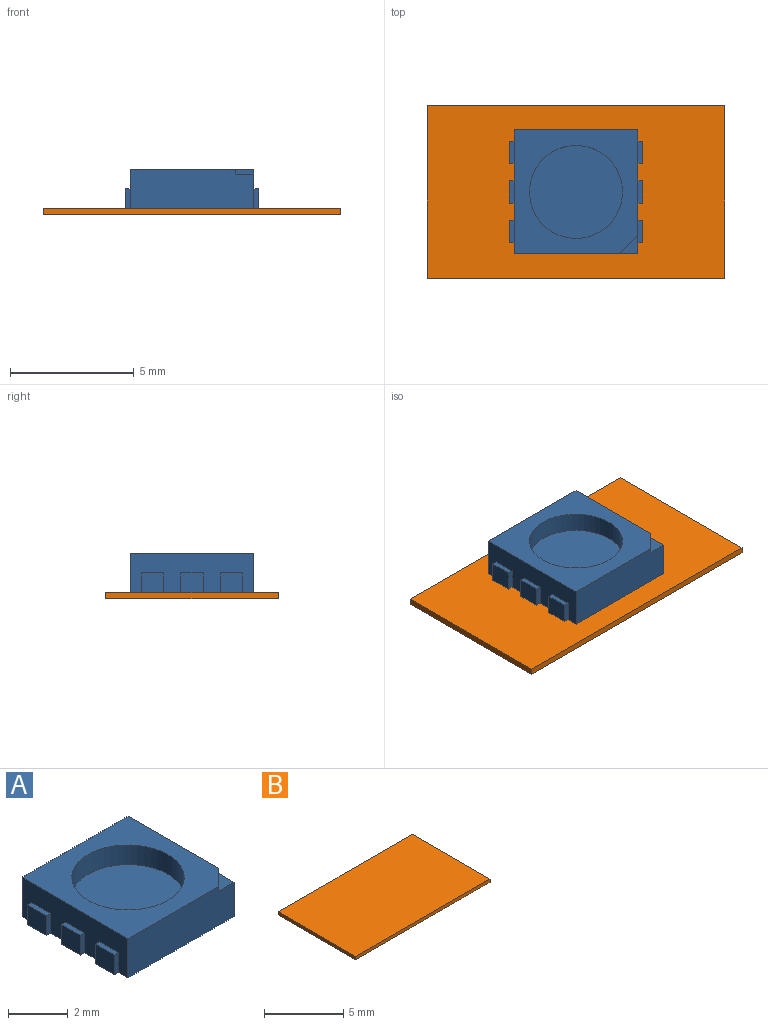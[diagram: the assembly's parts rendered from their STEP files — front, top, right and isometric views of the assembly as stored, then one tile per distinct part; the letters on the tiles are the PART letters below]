
ASSEMBLY  parts=2 mates=1
PART A: 34 faces, bbox 5.4x5x1.6 mm
  f0: plane 5x1.6mm, normal (1,0,0), area 5.7mm2, adj f1,f2,f4,f5,f18,f19,f21,f22
  f1: plane 5x1.6mm, normal (0,-1,0), area 7.9mm2, adj f0,f2,f3,f5,f30,f31
  f2: plane 5x5mm, normal (0,0,1), area 13.7mm2, adj f0,f1,f3,f4,f30,f32
  f3: plane 5x1.6mm, normal (-1,0,0), area 5.8mm2, adj f1,f2,f4,f5,f6,f7,f8,f10
  f4: plane 5x1.6mm, normal (0,1,0), area 8mm2, adj f0,f2,f3,f5
  f5: plane 5.4x5mm, normal (0,0,-1), area 26.1mm2, adj f0,f1,f3,f4,f6,f7,f9,f11
  f6: plane 0.8x0.2mm, normal (0,-1,0), area 0.2mm2, adj f3,f5,f8,f9
  f7: plane 0.8x0.2mm, normal (0,1,0), area 0.2mm2, adj f3,f5,f8,f9
  f8: plane 0.9x0.2mm, normal (0,0,1), area 0.2mm2, adj f3,f6,f7,f9
  f9: plane 0.9x0.8mm, normal (-1,0,0), area 0.7mm2, adj f5,f6,f7,f8
  f10: plane 0.9x0.2mm, normal (0,0,1), area 0.2mm2, adj f3,f11,f12,f13
  f11: plane 0.8x0.2mm, normal (0,1,0), area 0.2mm2, adj f3,f5,f10,f13
  f12: plane 0.8x0.2mm, normal (0,-1,0), area 0.2mm2, adj f3,f5,f10,f13
  f13: plane 0.9x0.8mm, normal (-1,0,0), area 0.7mm2, adj f5,f10,f11,f12
  f14: plane 0.9x0.2mm, normal (0,0,1), area 0.2mm2, adj f3,f15,f16,f17
  f15: plane 0.8x0.2mm, normal (0,1,0), area 0.2mm2, adj f3,f5,f14,f17
  f16: plane 0.8x0.2mm, normal (0,-1,0), area 0.2mm2, adj f3,f5,f14,f17
  f17: plane 0.9x0.8mm, normal (-1,0,0), area 0.7mm2, adj f5,f14,f15,f16
  f18: plane 0.8x0.2mm, normal (0,-1,0), area 0.2mm2, adj f0,f5,f20,f21
  f19: plane 0.8x0.2mm, normal (0,1,0), area 0.2mm2, adj f0,f5,f20,f21
  f20: plane 0.9x0.8mm, normal (1,0,0), area 0.7mm2, adj f5,f18,f19,f21
  f21: plane 0.9x0.2mm, normal (0,0,1), area 0.2mm2, adj f0,f18,f19,f20
  f22: plane 0.8x0.2mm, normal (0,-1,0), area 0.2mm2, adj f0,f5,f24,f25
  f23: plane 0.8x0.2mm, normal (0,1,0), area 0.2mm2, adj f0,f5,f24,f25
  f24: plane 0.9x0.8mm, normal (1,0,0), area 0.7mm2, adj f5,f22,f23,f25
  f25: plane 0.9x0.2mm, normal (0,0,1), area 0.2mm2, adj f0,f22,f23,f24
  f26: plane 0.8x0.2mm, normal (0,-1,0), area 0.2mm2, adj f0,f5,f28,f29
  f27: plane 0.8x0.2mm, normal (0,1,0), area 0.2mm2, adj f0,f5,f28,f29
  f28: plane 0.9x0.8mm, normal (1,0,0), area 0.7mm2, adj f5,f26,f27,f29
  f29: plane 0.9x0.2mm, normal (0,0,1), area 0.2mm2, adj f0,f26,f27,f28
  f30: plane 0.75x0.75mm, normal (0.71,-0.71,0), area 0.2mm2, adj f0,f1,f2,f31
  f31: plane 0.75x0.75mm, normal (0,0,1), area 0.3mm2, adj f0,f1,f30
  f32: cylinder r=1.88mm len=3.75mm, axis (0,0,1), area 9.4mm2, adj f2,f33
  f33: plane 3.75x3.75mm, normal (0,0,1), area 11mm2, adj f32
PART B: 6 faces, bbox 12x6.9x0.3 mm
  f0: plane 6.94x0.25mm, normal (1,0,0), area 1.7mm2, adj f1,f3,f4,f5
  f1: plane 12x0.25mm, normal (0,1,0), area 3mm2, adj f0,f2,f4,f5
  f2: plane 6.94x0.25mm, normal (-1,0,0), area 1.7mm2, adj f1,f3,f4,f5
  f3: plane 12x0.25mm, normal (0,-1,0), area 3mm2, adj f0,f2,f4,f5
  f4: plane 12x6.94mm, normal (0,0,1), area 83.3mm2, adj f0,f1,f2,f3
  f5: plane 12x6.94mm, normal (0,0,-1), area 83.3mm2, adj f0,f1,f2,f3
PLACE A t=(4.9,5.07,2.56)mm
PLACE B t=(4.9,5.07,2.31)mm
MATE planar B.f4 <-> A.f32  axis (0,0,1) through (4.9,5.07,2.56)mm
